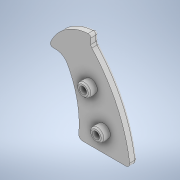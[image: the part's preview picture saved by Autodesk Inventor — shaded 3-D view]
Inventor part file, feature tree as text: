
AUTODESK INVENTOR PART (.ipt)
format: ipt  version: 2021 (Build 250183000, 183)  size: 181,248 bytes
history: native  units: in
note: dims shown in document units (in); Inventor stores cm internally (conversion verified against a paired STEP export)
features: chamfer x4, extrude x2, sketch x2, fillet x1
ambient origin geometry x8: Origin, YZ Plane, XZ Plane, XY Plane, X Axis, Y Axis, Z Axis, Center Point
bodies: Solid1 (feature_tree)
feature tree (9):
  extrude  "Extrusion1"  Depth=0.0787in
  fillet  "Fillet1"  Radius=0.0787in
  chamfer  "Chamfer1"  Distance=0.2362in
  chamfer  "Chamfer2"  Distance=0.0394in Angle=45.0deg
  extrude  "Extrusion2"  Depth=0.0394in TaperAngle=45.0deg
  chamfer  "Chamfer3"  [1 undecoded]
  chamfer  "Chamfer4"  [1 undecoded]
  sketch  "Sketch1"  dims[d0=0.2362in d1=0.0in d2=0.0787in]
  sketch  "Sketch2"  dims[d3=0.0984in d4=0.0787in d5=45.0deg d6=0.0984in d7=0.0787in d8=45.0deg d9=0.2362in d10=0.0in d11=0.0394in d12=0.0787in d13=45.0deg d14=0.0394in d15=0.0787in d16=45.0deg]
note: 2 required parameter values undecoded (feature->parameter linkage not recoverable at this tier; creation-order binding heuristic only, values carry confidence <= 0.55)
